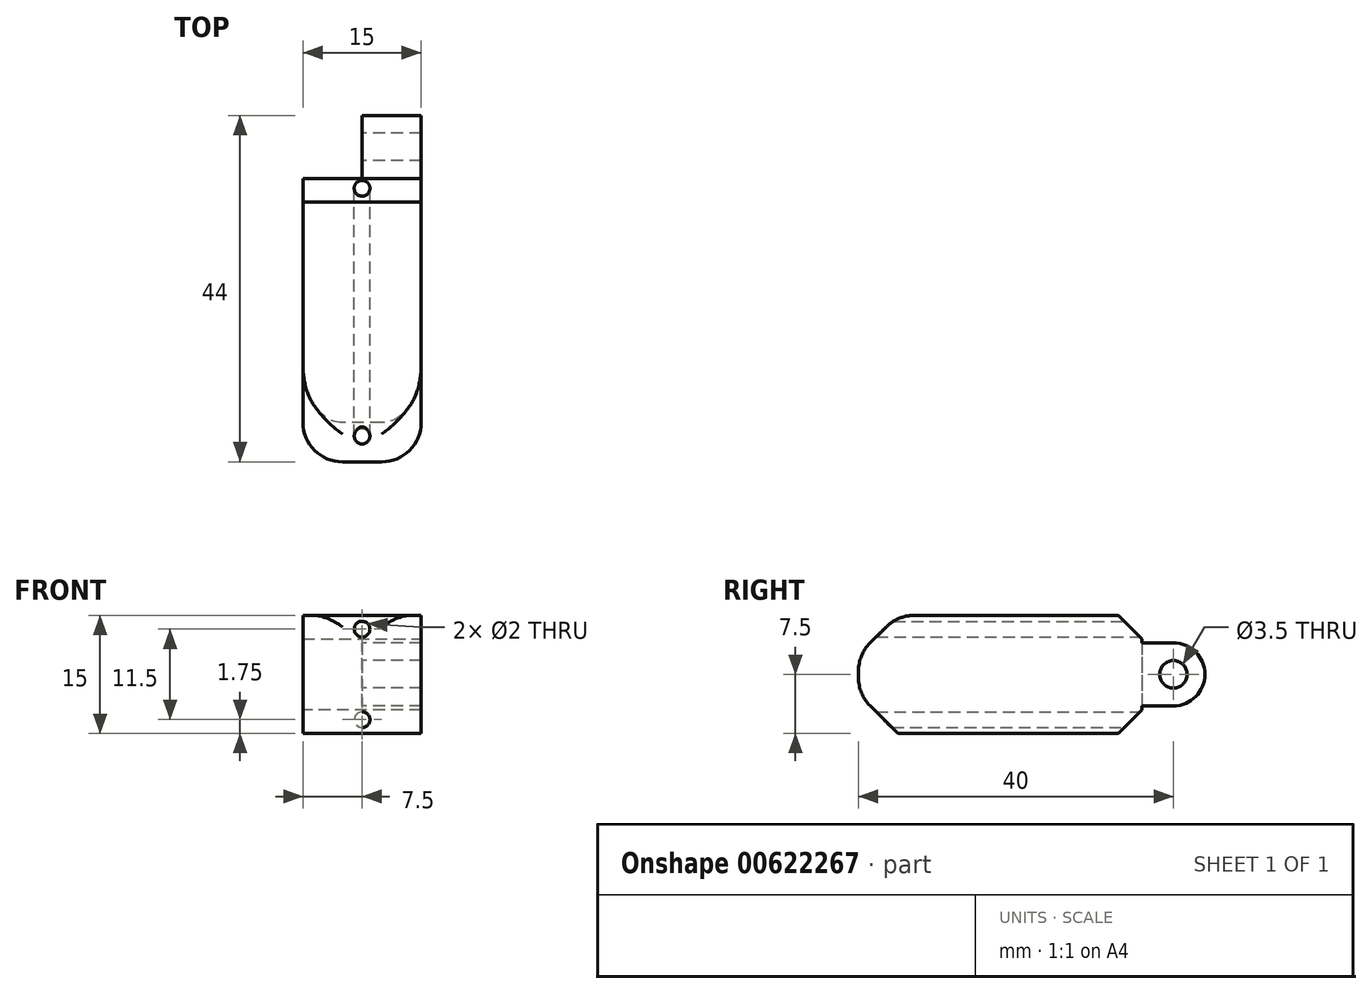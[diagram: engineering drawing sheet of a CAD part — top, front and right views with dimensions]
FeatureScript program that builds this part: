
annotation { "Feature Type Name" : "Feature", "Feature Type Description" : "" }
export const myFeature = defineFeature(function(context is Context, id is Id, definition is map)
    precondition{}
    {
        {
            var Q0;
            Q0=qCreatedBy(makeId("Right.planeOp"),FACE);
            var sketch = newSketch(context, id + "F0", { "sketchPlane" : qUnion([Q0])});
            skLineSegment(sketch, "E0.bottom", {"start": v(20, 4) * mm, "end": v(-20, 4) * mm});
            skLineSegment(sketch, "E0.top", {"start": v(20, -4) * mm, "end": v(-20, -4) * mm});
            skLineSegment(sketch, "E0.left", {"start": v(20, 4) * mm, "end": v(20, -4) * mm});
            skLineSegment(sketch, "E0.right", {"start": v(-20, 4) * mm, "end": v(-20, -4) * mm});
            skPoint(sketch, "E0.middle", {"position": v(0, 0) * mm});
            skCircle(sketch, "E1", {"center": v(20, 0) * mm, "radius": 4 * mm});
            skLineSegment(sketch, "E2.bottom", {"start": v(16, 7.5) * mm, "end": v(-16, 7.5) * mm});
            skLineSegment(sketch, "E2.top", {"start": v(16, -7.5) * mm, "end": v(-16, -7.5) * mm});
            skLineSegment(sketch, "E2.left", {"start": v(16, 7.5) * mm, "end": v(16, -7.5) * mm});
            skLineSegment(sketch, "E2.right", {"start": v(-16, 7.5) * mm, "end": v(-16, -7.5) * mm});
            skCircle(sketch, "E3", {"center": v(20, 0) * mm, "radius": 1.75 * mm});
            skLineSegment(sketch, "E4.bottom", {"start": v(-16, 7.5) * mm, "end": v(-20, 7.5) * mm});
            skLineSegment(sketch, "E4.top", {"start": v(-16, -7.5) * mm, "end": v(-20, -7.5) * mm});
            skLineSegment(sketch, "E4.right", {"start": v(-20, 7.5) * mm, "end": v(-20, -7.5) * mm});
            skSolve(sketch);
        }
        {
            var Q0;
            {var subQ5=sQuery(id+"F0.wireOp",EDGE,"E4.bottom");Q0=makeQuery(id+"F0.imprint","IMPRINT",FACE,{"disambiguationData":[TD([[makeQuery(id+"F0.imprint","IMPRINT",EDGE,{"derivedFrom":subQ5}),1.0]])]});}
            var Q1;
            {var subQ0=sQuery(id+"F0.wireOp",EDGE,"E4.right");var subQ1=sQuery(id+"F0.wireOp",EDGE,"E0.bottom");var subQ2=makeQuery(id+"F0.imprint","INTERSECT",VERTEX,{"derivedFrom":[subQ1,subQ0]});Q1=makeQuery(id+"F0.imprint","IMPRINT",FACE,{"disambiguationData":[TD([[makeQuery(id+"F0.imprint","IMPRINT",EDGE,{"disambiguationData":[TD([[subQ2,1.0]])],"derivedFrom":subQ1}),1.0]])]});}
            var Q2;
            {var subQ5=sQuery(id+"F0.wireOp",EDGE,"E4.top");Q2=makeQuery(id+"F0.imprint","IMPRINT",FACE,{"disambiguationData":[TD([[makeQuery(id+"F0.imprint","IMPRINT",EDGE,{"derivedFrom":subQ5}),-1.0]])]});}
            var Q3;
            {var subQ5=sQuery(id+"F0.wireOp",EDGE,"E2.top");Q3=makeQuery(id+"F0.imprint","IMPRINT",FACE,{"disambiguationData":[TD([[makeQuery(id+"F0.imprint","IMPRINT",EDGE,{"derivedFrom":subQ5}),-1.0]])]});}
            var Q4;
            {var subQ0=sQuery(id+"F0.wireOp",EDGE,"E2.left");var subQ1=sQuery(id+"F0.wireOp",EDGE,"E0.bottom");var subQ2=makeQuery(id+"F0.imprint","INTERSECT",VERTEX,{"derivedFrom":[subQ1,subQ0]});Q4=makeQuery(id+"F0.imprint","IMPRINT",FACE,{"disambiguationData":[TD([[makeQuery(id+"F0.imprint","IMPRINT",EDGE,{"disambiguationData":[TD([[subQ2,-1.0]])],"derivedFrom":subQ1}),1.0]])]});}
            var Q5;
            {var subQ5=sQuery(id+"F0.wireOp",EDGE,"E2.bottom");Q5=makeQuery(id+"F0.imprint","IMPRINT",FACE,{"disambiguationData":[TD([[makeQuery(id+"F0.imprint","IMPRINT",EDGE,{"derivedFrom":subQ5}),1.0]])]});}
            extrude(context, id + "F1", {"entities" : qUnion([Q0, Q1, Q2, Q3, Q4, Q5]), "endBound" : BoundingType.SYMMETRIC, "depth" : 15 * mm, "offsetDistance" : 25 * mm});
        }
        {
            var Q0;
            {var subQ1=sQuery(id+"F0.wireOp",EDGE,"E0.left");var subQ5=sQuery(id+"F0.wireOp",EDGE,"E3");var subQ7=makeQuery(id+"F0.imprint","INTERSECT",VERTEX,{"disambiguationData":[OD(0.0)],"derivedFrom":[subQ1,subQ5]});Q0=makeQuery(id+"F0.imprint","IMPRINT",FACE,{"disambiguationData":[TD([[makeQuery(id+"F0.imprint","IMPRINT",EDGE,{"disambiguationData":[TD([[subQ7,-1.0]])],"derivedFrom":subQ5}),-1.0]])]});}
            var Q1;
            {var subQ1=sQuery(id+"F0.wireOp",EDGE,"E0.bottom");var subQ3=sQuery(id+"F0.wireOp",EDGE,"E2.left");var subQ4=makeQuery(id+"F0.imprint","INTERSECT",VERTEX,{"derivedFrom":[subQ1,subQ3]});Q1=makeQuery(id+"F0.imprint","IMPRINT",FACE,{"disambiguationData":[TD([[makeQuery(id+"F0.imprint","IMPRINT",EDGE,{"disambiguationData":[TD([[subQ4,-1.0]])],"derivedFrom":subQ3}),1.0]])]});}
            var Q2;
            {var subQ1=sQuery(id+"F0.wireOp",EDGE,"E0.top");var subQ3=sQuery(id+"F0.wireOp",EDGE,"E2.left");var subQ4=makeQuery(id+"F0.imprint","INTERSECT",VERTEX,{"derivedFrom":[subQ1,subQ3]});Q2=makeQuery(id+"F0.imprint","IMPRINT",FACE,{"disambiguationData":[TD([[makeQuery(id+"F0.imprint","IMPRINT",EDGE,{"disambiguationData":[TD([[subQ4,1.0]])],"derivedFrom":subQ3}),1.0]])]});}
            var Q3;
            {var subQ1=sQuery(id+"F0.wireOp",EDGE,"E0.left");var subQ3=sQuery(id+"F0.wireOp",EDGE,"E3");var subQ4=makeQuery(id+"F0.imprint","INTERSECT",VERTEX,{"disambiguationData":[OD(0.0)],"derivedFrom":[subQ1,subQ3]});Q3=makeQuery(id+"F0.imprint","IMPRINT",FACE,{"disambiguationData":[TD([[makeQuery(id+"F0.imprint","IMPRINT",EDGE,{"disambiguationData":[TD([[subQ4,1.0]])],"derivedFrom":subQ3}),-1.0]])]});}
            extrude(context, id + "F2", {"entities" : qUnion([Q0, Q1, Q2, Q3]), "operationType" : NewBodyOperationType.ADD, "depth" : 7.5 * mm, "offsetDistance" : 25 * mm});
        }
        {
            var Q0;
            Q0=makeQuery(id+"F1.opExtrude","SWEPT_FACE",FACE,{"disambiguationData":[OSD([sQuery(id+"F0.wireOp",EDGE,"E2.left")])]});
            var sketch = newSketch(context, id + "F3", { "sketchPlane" : qUnion([Q0])});
            skLineSegment(sketch, "E5", {"start": v(0, 7.5) * mm, "end": v(0, 4) * mm});
            skCircle(sketch, "E6", {"center": v(0, 5.75) * mm, "radius": 1 * mm});
            skLineSegment(sketch, "E7", {"start": v(0, -4) * mm, "end": v(0, -7.5) * mm});
            skCircle(sketch, "E8", {"center": v(0, -5.75) * mm, "radius": 1 * mm});
            skSolve(sketch);
        }
        {
            var Q0;
            Q0 = qSketchRegion(id + "F3", true);
            extrude(context, id + "F4", {"entities" : qUnion([Q0]), "operationType" : NewBodyOperationType.REMOVE, "oppositeDirection" : true, "depth" : 40 * mm, "offsetDistance" : 25 * mm});
        }
        {
            var Q0;
            Q0=makeQuery(id+"F1.opExtrude","SWEPT_EDGE",EDGE,{"disambiguationData":[OSD([sQuery(id+"F0.wireOp",EDGE,"E2.bottom"),sQuery(id+"F0.wireOp",EDGE,"E2.left")])]});
            var Q1;
            Q1=makeQuery(id+"F1.opExtrude","SWEPT_EDGE",EDGE,{"disambiguationData":[OSD([sQuery(id+"F0.wireOp",EDGE,"E2.top"),sQuery(id+"F0.wireOp",EDGE,"E2.left")])]});
            chamfer(context, id + "F5", {"entities" : qUnion([Q0, Q1]), "width" : 3 * mm, "tangentPropagation" : true});
        }
        {
            var Q0;
            Q0=makeQuery(id+"F1.opExtrude","SWEPT_EDGE",EDGE,{"disambiguationData":[OSD([sQuery(id+"F0.wireOp",EDGE,"E4.bottom"),sQuery(id+"F0.wireOp",EDGE,"E4.right")])]});
            var Q1;
            Q1=makeQuery(id+"F1.opExtrude","SWEPT_EDGE",EDGE,{"disambiguationData":[OSD([sQuery(id+"F0.wireOp",EDGE,"E4.top"),sQuery(id+"F0.wireOp",EDGE,"E4.right")])]});
            chamfer(context, id + "F6", {"entities" : qUnion([Q0, Q1]), "width" : 5 * mm, "tangentPropagation" : true});
        }
        {
            var Q0;
            {var subQ0=sQuery(id+"F0.wireOp",EDGE,"E4.right");var subQ1=sQuery(id+"F0.wireOp",EDGE,"E4.bottom");Q0=makeQuery(id+"F6.opChamfer","BLEND_EDGE",EDGE,{"blendedFrom":[makeQuery(id+"F1.opExtrude","SWEPT_EDGE",EDGE,{"disambiguationData":[OSD([subQ1,subQ0])]}),makeQuery(id+"F1.opExtrude","CAP_FACE",FACE,{"disambiguationData":[OSD([sQuery(id+"F0.wireOp",EDGE,"E2.bottom"),sQuery(id+"F0.wireOp",EDGE,"E2.top"),sQuery(id+"F0.wireOp",EDGE,"E2.left"),subQ1,sQuery(id+"F0.wireOp",EDGE,"E4.top"),subQ0])],"isStart":true})],"blendedInto":[makeQuery(id+"F1.opExtrude","CAP_FACE",FACE,{"disambiguationData":[OSD([sQuery(id+"F0.wireOp",EDGE,"E2.bottom"),sQuery(id+"F0.wireOp",EDGE,"E2.top"),sQuery(id+"F0.wireOp",EDGE,"E2.left"),subQ1,sQuery(id+"F0.wireOp",EDGE,"E4.top"),subQ0])],"isStart":true})]});}
            var Q1;
            {var subQ0=sQuery(id+"F0.wireOp",EDGE,"E4.bottom");Q1=makeQuery(id+"F6.opChamfer","BLEND_EDGE",EDGE,{"blendedFrom":[makeQuery(id+"F1.opExtrude","SWEPT_EDGE",EDGE,{"disambiguationData":[OSD([subQ0,sQuery(id+"F0.wireOp",EDGE,"E4.right")])]}),makeQuery(id+"F1.opExtrude","SWEPT_FACE",FACE,{"disambiguationData":[OSD([sQuery(id+"F0.wireOp",EDGE,"E2.bottom"),subQ0])]})],"blendedInto":[makeQuery(id+"F1.opExtrude","SWEPT_FACE",FACE,{"disambiguationData":[OSD([sQuery(id+"F0.wireOp",EDGE,"E2.bottom"),subQ0])]})]});}
            var Q2;
            {var subQ0=sQuery(id+"F0.wireOp",EDGE,"E4.right");Q2=makeQuery(id+"F6.opChamfer","BLEND_EDGE",EDGE,{"blendedFrom":[makeQuery(id+"F1.opExtrude","SWEPT_EDGE",EDGE,{"disambiguationData":[OSD([sQuery(id+"F0.wireOp",EDGE,"E4.bottom"),subQ0])]}),makeQuery(id+"F1.opExtrude","SWEPT_FACE",FACE,{"disambiguationData":[OSD([subQ0])]})],"blendedInto":[makeQuery(id+"F1.opExtrude","SWEPT_FACE",FACE,{"disambiguationData":[OSD([subQ0])]})]});}
            var Q3;
            Q3=makeQuery(id+"F1.opExtrude","CAP_EDGE",EDGE,{"disambiguationData":[OSD([sQuery(id+"F0.wireOp",EDGE,"E4.right")])],"isStart":true});
            var Q4;
            {var subQ0=sQuery(id+"F0.wireOp",EDGE,"E4.right");var subQ1=sQuery(id+"F0.wireOp",EDGE,"E4.top");Q4=makeQuery(id+"F6.opChamfer","BLEND_EDGE",EDGE,{"blendedFrom":[makeQuery(id+"F1.opExtrude","SWEPT_EDGE",EDGE,{"disambiguationData":[OSD([subQ1,subQ0])]}),makeQuery(id+"F1.opExtrude","CAP_FACE",FACE,{"disambiguationData":[OSD([sQuery(id+"F0.wireOp",EDGE,"E2.bottom"),sQuery(id+"F0.wireOp",EDGE,"E2.top"),sQuery(id+"F0.wireOp",EDGE,"E2.left"),sQuery(id+"F0.wireOp",EDGE,"E4.bottom"),subQ1,subQ0])],"isStart":true})],"blendedInto":[makeQuery(id+"F1.opExtrude","CAP_FACE",FACE,{"disambiguationData":[OSD([sQuery(id+"F0.wireOp",EDGE,"E2.bottom"),sQuery(id+"F0.wireOp",EDGE,"E2.top"),sQuery(id+"F0.wireOp",EDGE,"E2.left"),sQuery(id+"F0.wireOp",EDGE,"E4.bottom"),subQ1,subQ0])],"isStart":true})]});}
            var Q5;
            {var subQ0=sQuery(id+"F0.wireOp",EDGE,"E4.right");var subQ1=sQuery(id+"F0.wireOp",EDGE,"E4.top");Q5=makeQuery(id+"F6.opChamfer","BLEND_EDGE",EDGE,{"blendedFrom":[makeQuery(id+"F1.opExtrude","SWEPT_EDGE",EDGE,{"disambiguationData":[OSD([subQ1,subQ0])]}),makeQuery(id+"F1.opExtrude","CAP_FACE",FACE,{"disambiguationData":[OSD([sQuery(id+"F0.wireOp",EDGE,"E2.bottom"),sQuery(id+"F0.wireOp",EDGE,"E2.top"),sQuery(id+"F0.wireOp",EDGE,"E2.left"),sQuery(id+"F0.wireOp",EDGE,"E4.bottom"),subQ1,subQ0])],"isStart":false})],"blendedInto":[makeQuery(id+"F1.opExtrude","CAP_FACE",FACE,{"disambiguationData":[OSD([sQuery(id+"F0.wireOp",EDGE,"E2.bottom"),sQuery(id+"F0.wireOp",EDGE,"E2.top"),sQuery(id+"F0.wireOp",EDGE,"E2.left"),sQuery(id+"F0.wireOp",EDGE,"E4.bottom"),subQ1,subQ0])],"isStart":false})]});}
            var Q6;
            Q6=makeQuery(id+"F1.opExtrude","CAP_EDGE",EDGE,{"disambiguationData":[OSD([sQuery(id+"F0.wireOp",EDGE,"E4.right")])],"isStart":false});
            var Q7;
            {var subQ0=sQuery(id+"F0.wireOp",EDGE,"E4.right");var subQ1=sQuery(id+"F0.wireOp",EDGE,"E4.bottom");Q7=makeQuery(id+"F6.opChamfer","BLEND_EDGE",EDGE,{"blendedFrom":[makeQuery(id+"F1.opExtrude","SWEPT_EDGE",EDGE,{"disambiguationData":[OSD([subQ1,subQ0])]}),makeQuery(id+"F1.opExtrude","CAP_FACE",FACE,{"disambiguationData":[OSD([sQuery(id+"F0.wireOp",EDGE,"E2.bottom"),sQuery(id+"F0.wireOp",EDGE,"E2.top"),sQuery(id+"F0.wireOp",EDGE,"E2.left"),subQ1,sQuery(id+"F0.wireOp",EDGE,"E4.top"),subQ0])],"isStart":false})],"blendedInto":[makeQuery(id+"F1.opExtrude","CAP_FACE",FACE,{"disambiguationData":[OSD([sQuery(id+"F0.wireOp",EDGE,"E2.bottom"),sQuery(id+"F0.wireOp",EDGE,"E2.top"),sQuery(id+"F0.wireOp",EDGE,"E2.left"),subQ1,sQuery(id+"F0.wireOp",EDGE,"E4.top"),subQ0])],"isStart":false})]});}
            var Q8;
            {var subQ0=sQuery(id+"F0.wireOp",EDGE,"E4.right");Q8=makeQuery(id+"F6.opChamfer","BLEND_EDGE",EDGE,{"blendedFrom":[makeQuery(id+"F1.opExtrude","SWEPT_EDGE",EDGE,{"disambiguationData":[OSD([sQuery(id+"F0.wireOp",EDGE,"E4.top"),subQ0])]}),makeQuery(id+"F1.opExtrude","SWEPT_FACE",FACE,{"disambiguationData":[OSD([subQ0])]})],"blendedInto":[makeQuery(id+"F1.opExtrude","SWEPT_FACE",FACE,{"disambiguationData":[OSD([subQ0])]})]});}
            fillet(context, id + "F7", {"entities" : qUnion([Q0, Q1, Q2, Q3, Q4, Q5, Q6, Q7, Q8]), "radius" : 5 * mm, "tangentPropagation" : true, "allowEdgeOverflow" : false});
        }
    });
